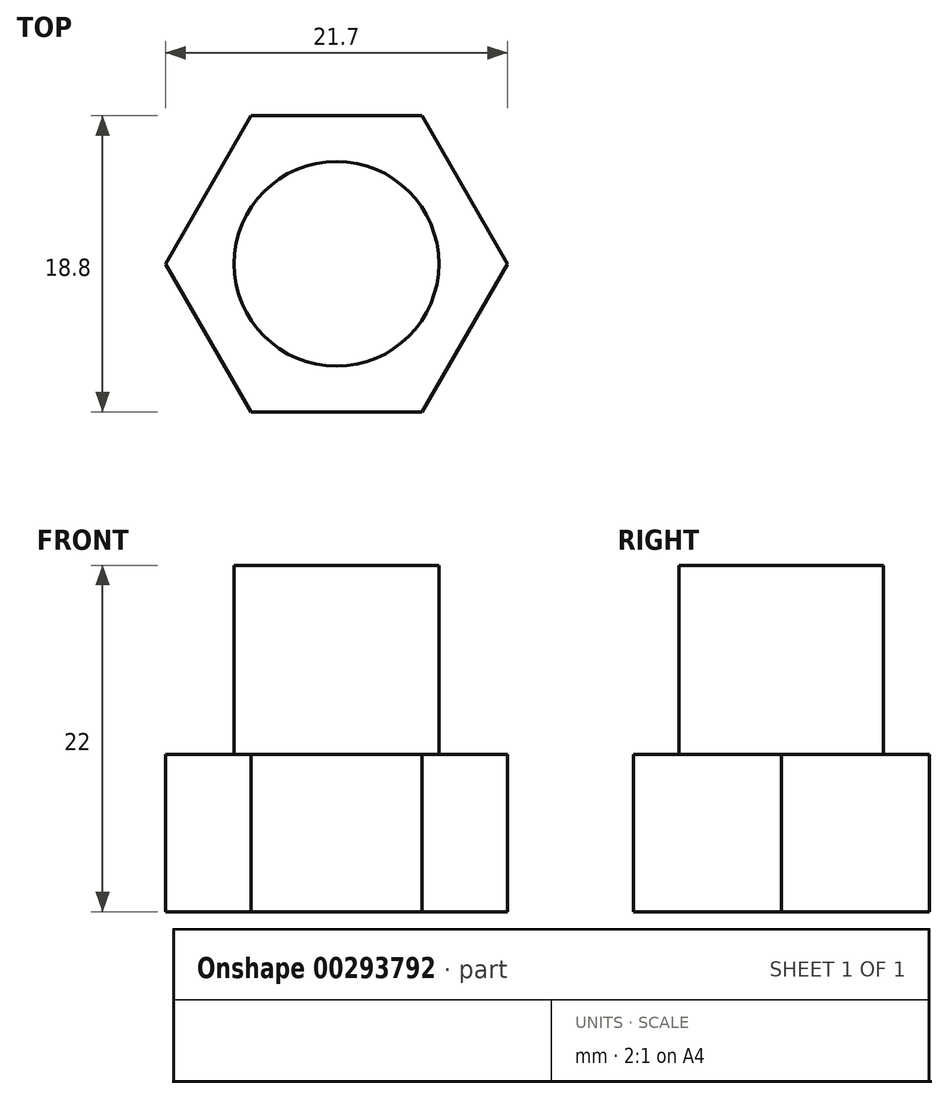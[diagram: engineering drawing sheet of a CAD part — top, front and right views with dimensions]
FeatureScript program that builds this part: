
annotation { "Feature Type Name" : "Feature", "Feature Type Description" : "" }
export const myFeature = defineFeature(function(context is Context, id is Id, definition is map)
    precondition{}
    {
        {
            var Q0;
            Q0=qCreatedBy(makeId("Top.planeOp"),FACE);
            var sketch = newSketch(context, id + "F0", { "sketchPlane" : qUnion([Q0])});
            skCircle(sketch, "E0.cCircle", {"center": v(0, 0) * mm, "radius": 9.4 * mm, "construction": true});
            skLineSegment(sketch, "E0.0", {"start": v(-5.43, 9.4) * mm, "end": v(5.43, 9.4) * mm});
            skLineSegment(sketch, "E0.1", {"start": v(5.43, 9.4) * mm, "end": v(10.85, 0) * mm});
            skLineSegment(sketch, "E0.2", {"start": v(10.85, 0) * mm, "end": v(5.43, -9.4) * mm});
            skLineSegment(sketch, "E0.3", {"start": v(5.43, -9.4) * mm, "end": v(-5.43, -9.4) * mm});
            skLineSegment(sketch, "E0.4", {"start": v(-5.43, -9.4) * mm, "end": v(-10.85, 0) * mm});
            skLineSegment(sketch, "E0.5", {"start": v(-10.85, 0) * mm, "end": v(-5.43, 9.4) * mm});
            skPoint(sketch, "E0.0.midPoint", {"position": v(0, 9.4) * mm});
            skSolve(sketch);
        }
        {
            var Q0;
            Q0 = qSketchRegion(id + "F0", true);
            extrude(context, id + "F1", {"entities" : qUnion([Q0]), "depth" : 10 * mm, "offsetDistance" : 25 * mm});
        }
        {
            var Q0;
            Q0=makeQuery(id+"F1.opExtrude","CAP_FACE",FACE,{"disambiguationData":[OSD([sQuery(id+"F0.wireOp",EDGE,"E0.0"),sQuery(id+"F0.wireOp",EDGE,"E0.1"),sQuery(id+"F0.wireOp",EDGE,"E0.2"),sQuery(id+"F0.wireOp",EDGE,"E0.3"),sQuery(id+"F0.wireOp",EDGE,"E0.4"),sQuery(id+"F0.wireOp",EDGE,"E0.5")])],"isStart":false});
            var sketch = newSketch(context, id + "F2", { "sketchPlane" : qUnion([Q0])});
            skCircle(sketch, "E1", {"center": v(0, 0) * mm, "radius": 6.5 * mm});
            skSolve(sketch);
        }
        {
            var Q0;
            Q0 = qSketchRegion(id + "F2", true);
            extrude(context, id + "F3", {"entities" : qUnion([Q0]), "operationType" : NewBodyOperationType.ADD, "depth" : 12 * mm, "offsetDistance" : 25 * mm});
        }
    });
